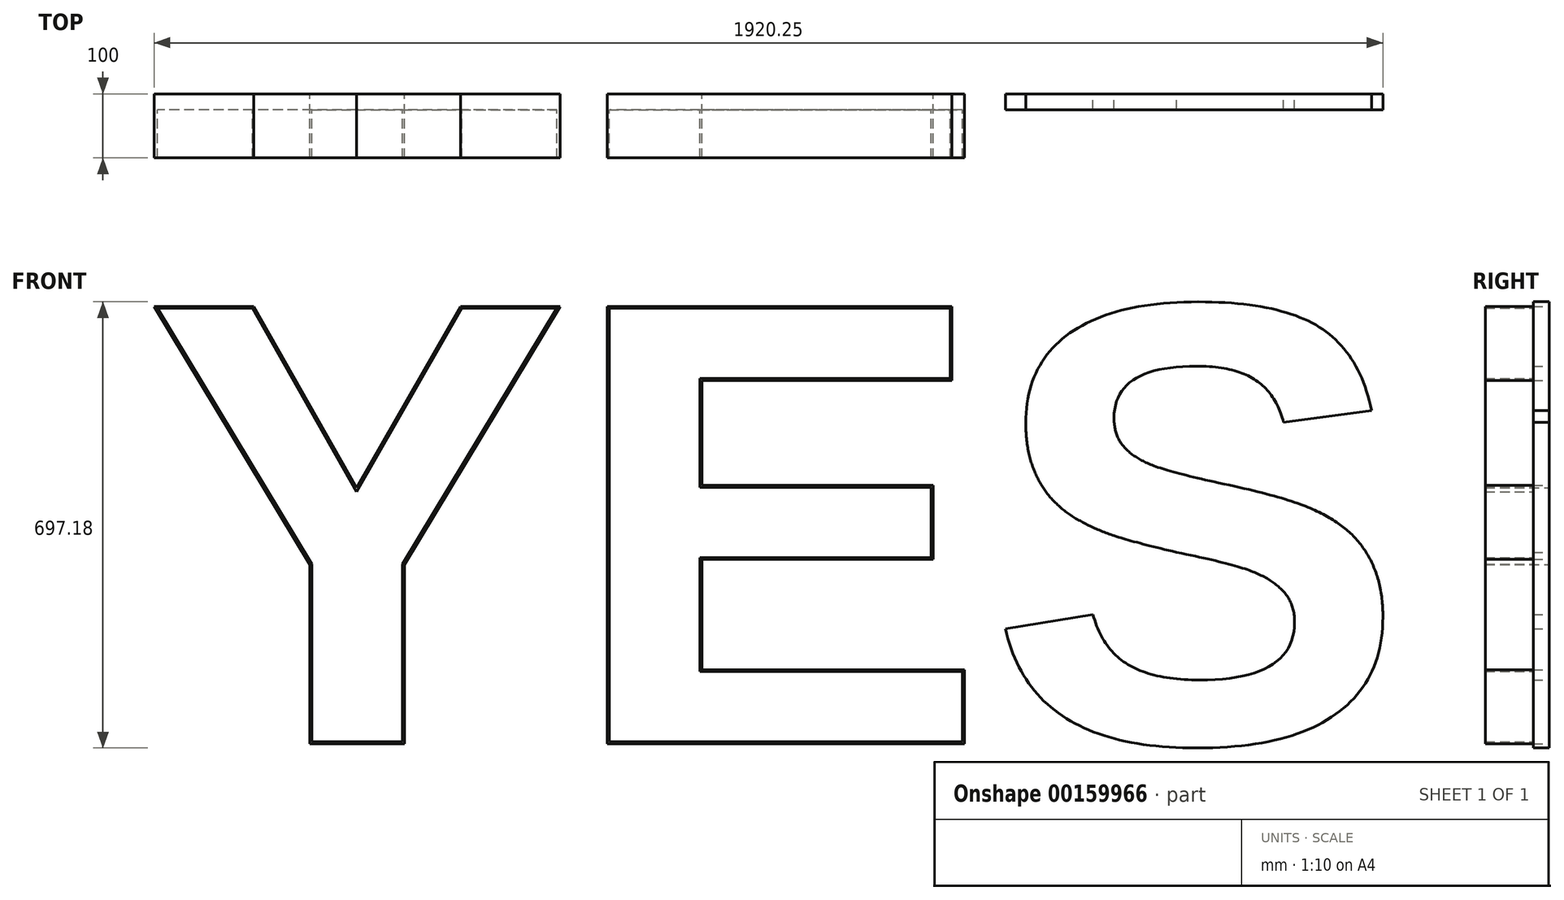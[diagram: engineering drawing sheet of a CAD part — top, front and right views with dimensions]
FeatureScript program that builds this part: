
annotation { "Feature Type Name" : "Feature", "Feature Type Description" : "" }
export const myFeature = defineFeature(function(context is Context, id is Id, definition is map)
    precondition{}
    {
        {
            var Q0;
            Q0=qCreatedBy(makeId("Front.planeOp"),FACE);
            var sketch = newSketch(context, id + "F0", { "sketchPlane" : qUnion([Q0])});
            skText(sketch, "E0", { "text": "YES", "fontName": "Arimo-Bold.ttf"});
            const initialGuessF0  = {"E0": [0, -0.70887, 1, 0, 0.70887]};
            skSetInitialGuess(sketch, initialGuessF0);
            skSolve(sketch);
        }
        {
            var Q0;
            Q0 = qSketchRegion(id + "F0", true);
            extrude(context, id + "F1", {"entities" : qUnion([Q0]), "depth" : 25 * mm});
        }
        {
            var Q0;
            Q0=qCreatedBy(makeId("Front.planeOp"),FACE);
            var sketch = newSketch(context, id + "F2", { "sketchPlane" : qUnion([Q0])});
            skLineSegment(sketch, "E1.0.0", {"start": v(399.5, -708.87) * mm, "end": v(399.5, -431.04) * mm});
            skLineSegment(sketch, "E1.0.1", {"start": v(399.5, -431.04) * mm, "end": v(640.87, -31.54) * mm});
            skLineSegment(sketch, "E1.0.2", {"start": v(640.87, -31.54) * mm, "end": v(492.27, -31.54) * mm});
            skLineSegment(sketch, "E1.0.3", {"start": v(492.27, -31.54) * mm, "end": v(327.82, -317.98) * mm});
            skLineSegment(sketch, "E1.0.4", {"start": v(327.82, -317.98) * mm, "end": v(165.37, -31.54) * mm});
            skLineSegment(sketch, "E1.0.5", {"start": v(165.37, -31.54) * mm, "end": v(16.77, -31.54) * mm});
            skLineSegment(sketch, "E1.0.6", {"start": v(16.77, -31.54) * mm, "end": v(258.13, -431.04) * mm});
            skLineSegment(sketch, "E1.0.7", {"start": v(258.13, -431.04) * mm, "end": v(258.13, -708.87) * mm});
            skLineSegment(sketch, "E1.0.8", {"start": v(258.13, -708.87) * mm, "end": v(399.5, -708.87) * mm});
            skLineSegment(sketch, "E2.0", {"start": v(646.2, -28.54) * mm, "end": v(490.53, -28.54) * mm});
            skLineSegment(sketch, "E2.1", {"start": v(402.5, -431.88) * mm, "end": v(646.2, -28.54) * mm});
            skLineSegment(sketch, "E2.2", {"start": v(490.53, -28.54) * mm, "end": v(327.84, -311.92) * mm});
            skLineSegment(sketch, "E2.3", {"start": v(402.5, -711.87) * mm, "end": v(402.5, -431.88) * mm});
            skLineSegment(sketch, "E2.4", {"start": v(255.13, -711.87) * mm, "end": v(402.5, -711.87) * mm});
            skLineSegment(sketch, "E2.5", {"start": v(327.84, -311.92) * mm, "end": v(167.12, -28.54) * mm});
            skLineSegment(sketch, "E2.6", {"start": v(167.12, -28.54) * mm, "end": v(11.45, -28.54) * mm});
            skLineSegment(sketch, "E2.7", {"start": v(11.45, -28.54) * mm, "end": v(255.13, -431.88) * mm});
            skLineSegment(sketch, "E2.8", {"start": v(255.13, -431.88) * mm, "end": v(255.13, -711.87) * mm});
            skSolve(sketch);
        }
        {
            var Q0;
            Q0 = qSketchRegion(id + "F2", true);
            extrude(context, id + "F3", {"entities" : qUnion([Q0]), "operationType" : NewBodyOperationType.ADD, "depth" : 100 * mm});
        }
        {
            var Q0;
            Q0=qCreatedBy(makeId("Front.planeOp"),FACE);
            var sketch = newSketch(context, id + "F4", { "sketchPlane" : qUnion([Q0])});
            skLineSegment(sketch, "E3.0.0", {"start": v(722.56, -31.54) * mm, "end": v(722.56, -708.87) * mm});
            skLineSegment(sketch, "E3.0.1", {"start": v(722.56, -708.87) * mm, "end": v(1274.98, -708.87) * mm});
            skLineSegment(sketch, "E3.0.2", {"start": v(1274.98, -708.87) * mm, "end": v(1274.98, -599.18) * mm});
            skLineSegment(sketch, "E3.0.3", {"start": v(1274.98, -599.18) * mm, "end": v(864.4, -599.18) * mm});
            skLineSegment(sketch, "E3.0.4", {"start": v(864.4, -599.18) * mm, "end": v(864.4, -420.9) * mm});
            skLineSegment(sketch, "E3.0.5", {"start": v(864.4, -420.9) * mm, "end": v(1225.9, -420.9) * mm});
            skLineSegment(sketch, "E3.0.6", {"start": v(1225.9, -420.9) * mm, "end": v(1225.9, -311.36) * mm});
            skLineSegment(sketch, "E3.0.7", {"start": v(1225.9, -311.36) * mm, "end": v(864.4, -311.36) * mm});
            skLineSegment(sketch, "E3.0.8", {"start": v(864.4, -311.36) * mm, "end": v(864.4, -141.07) * mm});
            skLineSegment(sketch, "E3.0.9", {"start": v(864.4, -141.07) * mm, "end": v(1255.29, -141.07) * mm});
            skLineSegment(sketch, "E3.0.10", {"start": v(1255.29, -141.07) * mm, "end": v(1255.29, -31.54) * mm});
            skLineSegment(sketch, "E3.0.11", {"start": v(1255.29, -31.54) * mm, "end": v(722.56, -31.54) * mm});
            skLineSegment(sketch, "E4.0", {"start": v(1258.29, -144.07) * mm, "end": v(1258.29, -28.54) * mm});
            skLineSegment(sketch, "E4.1", {"start": v(1277.98, -596.18) * mm, "end": v(867.4, -596.18) * mm});
            skLineSegment(sketch, "E4.2", {"start": v(1277.98, -711.87) * mm, "end": v(1277.98, -596.18) * mm});
            skLineSegment(sketch, "E4.3", {"start": v(719.56, -711.87) * mm, "end": v(1277.98, -711.87) * mm});
            skLineSegment(sketch, "E4.4", {"start": v(719.56, -28.54) * mm, "end": v(719.56, -711.87) * mm});
            skLineSegment(sketch, "E4.5", {"start": v(867.4, -596.18) * mm, "end": v(867.4, -423.9) * mm});
            skLineSegment(sketch, "E4.6", {"start": v(1258.29, -28.54) * mm, "end": v(719.56, -28.54) * mm});
            skLineSegment(sketch, "E4.7", {"start": v(867.4, -423.9) * mm, "end": v(1228.9, -423.9) * mm});
            skLineSegment(sketch, "E4.8", {"start": v(1228.9, -423.9) * mm, "end": v(1228.9, -308.36) * mm});
            skLineSegment(sketch, "E4.9", {"start": v(1228.9, -308.36) * mm, "end": v(867.4, -308.36) * mm});
            skLineSegment(sketch, "E4.10", {"start": v(867.4, -308.36) * mm, "end": v(867.4, -144.07) * mm});
            skLineSegment(sketch, "E4.11", {"start": v(867.4, -144.07) * mm, "end": v(1258.29, -144.07) * mm});
            skSolve(sketch);
        }
        {
            var Q0;
            Q0 = qSketchRegion(id + "F4", true);
            extrude(context, id + "F5", {"entities" : qUnion([Q0]), "operationType" : NewBodyOperationType.ADD, "depth" : 100 * mm});
        }
    });
